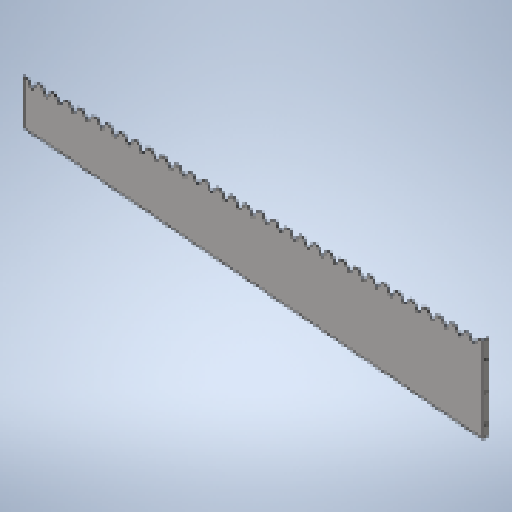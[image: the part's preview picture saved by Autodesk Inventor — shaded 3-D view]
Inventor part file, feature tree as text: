
AUTODESK INVENTOR PART (.ipt)
format: ipt  version: 2025 (Build 290162010, 162A)  size: 672,256 bytes
history: native  units: mm
features: other x6, sheet_metal_op x4, sketch x4, reference x3, extrude x2, fillet x1, pattern_linear x1
ambient origin geometry x8: Origin, YZ Plane, XZ Plane, XY Plane, X Axis, Y Axis, Z Axis, Center Point
bodies: Solid1 (feature_tree)
feature tree (21):
  sheet_metal_op  "Face1"
  extrude  "Extrusion2"  Depth=2000.0mm
  fillet  "Fillet2"  Radius=194.022673mm
  pattern_linear  "Rectangular Pattern1"  Count1=4  [1 undecoded]
  sheet_metal_op  "Flange1"
  extrude  "Extrusion3"  Depth=2.75mm
  other  "A-Side Definition"
  sketch  "Sketch1"  dims[d0=369.0mm d1=2000.0mm d2=194.022673mm]
  other  "Plate1"
  sketch  "Sketch3"  dims[d3=2.0mm]
  sketch  "Sketch4"  dims[d4=0.0mm]
  other  "Plate2"
  sheet_metal_op  "Bend1"
  sheet_metal_op  "Corner1"
  sketch  "Sketch6"  dims[d12=5.0mm d13=40.0mm d14=30.0mm d15=20.0mm d16=0.0mm d17=0.0mm d18=2.0mm d19=330.0mm d21=60.0mm d22=2.0mm d23=1.0mm d24=4.0mm d25=2.75mm d26=25.0mm d27=90.0deg d28=2.75mm d29=8.0mm d30=2.0mm d31=2.75mm d36=0.0mm d37=0.0mm d38=14.835299mm]
  reference  "Reference2"
  reference  "Reference3"
  reference  "Reference4"
  other  "ASY MSC 002 отстойник осветлитель.iam"
  other  "MSC 705 ridge 3:1"
  other  "Definition1"
note: 1 required parameter value undecoded (feature->parameter linkage not recoverable at this tier; creation-order binding heuristic only, values carry confidence <= 0.55)
